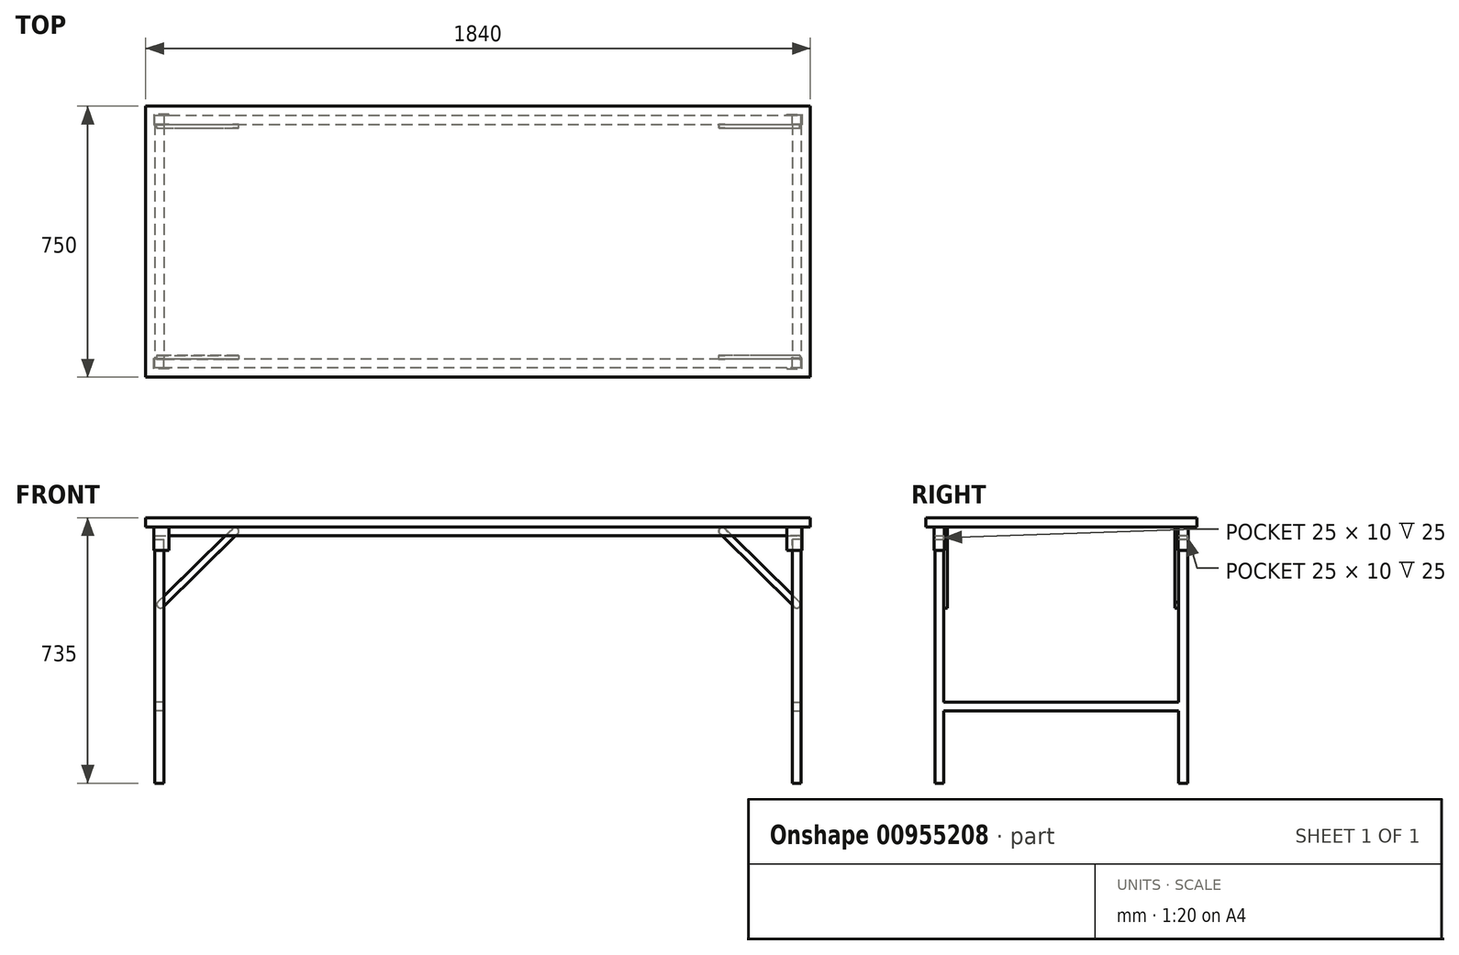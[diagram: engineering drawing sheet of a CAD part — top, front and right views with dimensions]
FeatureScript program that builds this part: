
annotation { "Feature Type Name" : "Feature", "Feature Type Description" : "" }
export const myFeature = defineFeature(function(context is Context, id is Id, definition is map)
    precondition{}
    {
        {
            var Q0;
            Q0=qCreatedBy(makeId("Top.planeOp"),FACE);
            var sketch = newSketch(context, id + "F0", { "sketchPlane" : qUnion([Q0])});
            skLineSegment(sketch, "E0.bottom", {"start": v(0, 0) * mm, "end": v(-1840, 0) * mm});
            skLineSegment(sketch, "E0.top", {"start": v(0, 750) * mm, "end": v(-1840, 750) * mm});
            skLineSegment(sketch, "E0.left", {"start": v(0, 0) * mm, "end": v(0, 750) * mm});
            skLineSegment(sketch, "E0.right", {"start": v(-1840, 0) * mm, "end": v(-1840, 750) * mm});
            skSolve(sketch);
        }
        {
            var Q0;
            Q0=makeQuery(id+"F0.imprint","IMPRINT",FACE,{"disambiguationData":[TD([[makeQuery(id+"F0.imprint","IMPRINT",EDGE,{"derivedFrom":sQuery(id+"F0.wireOp",EDGE,"E0.bottom")}),-1.0]])]});
            extrude(context, id + "F1", {"entities" : qUnion([Q0]), "depth" : 25 * mm, "offsetDistance" : 25 * mm});
        }
        {
            var Q0;
            Q0=makeQuery(id+"F1.opExtrude","CAP_FACE",FACE,{"disambiguationData":[OSD([sQuery(id+"F0.wireOp",EDGE,"E0.bottom"),sQuery(id+"F0.wireOp",EDGE,"E0.top"),sQuery(id+"F0.wireOp",EDGE,"E0.left"),sQuery(id+"F0.wireOp",EDGE,"E0.right")])],"isStart":true});
            var sketch = newSketch(context, id + "F2", { "sketchPlane" : qUnion([Q0])});
            skLineSegment(sketch, "E1.bottom", {"start": v(-25, -25) * mm, "end": v(-1815, -25) * mm});
            skLineSegment(sketch, "E1.top", {"start": v(-25, -50) * mm, "end": v(-1815, -50) * mm});
            skLineSegment(sketch, "E1.left", {"start": v(-25, -25) * mm, "end": v(-25, -50) * mm});
            skLineSegment(sketch, "E1.right", {"start": v(-1815, -25) * mm, "end": v(-1815, -50) * mm});
            skLineSegment(sketch, "E2.bottom", {"start": v(-1815, -700) * mm, "end": v(-25, -700) * mm});
            skLineSegment(sketch, "E2.top", {"start": v(-1815, -725) * mm, "end": v(-25, -725) * mm});
            skLineSegment(sketch, "E2.left", {"start": v(-1815, -700) * mm, "end": v(-1815, -725) * mm});
            skLineSegment(sketch, "E2.right", {"start": v(-25, -700) * mm, "end": v(-25, -725) * mm});
            skSolve(sketch);
        }
        {
            var Q0;
            Q0=qSketchRegion(id+"F2",true);
            extrude(context, id + "F3", {"entities" : qUnion([Q0]), "operationType" : NewBodyOperationType.ADD, "depth" : 25 * mm, "offsetDistance" : 25 * mm});
        }
        {
            var Q0;
            Q0=makeQuery(id+"F1.opExtrude","CAP_FACE",FACE,{"disambiguationData":[OSD([sQuery(id+"F0.wireOp",EDGE,"E0.bottom"),sQuery(id+"F0.wireOp",EDGE,"E0.top"),sQuery(id+"F0.wireOp",EDGE,"E0.left"),sQuery(id+"F0.wireOp",EDGE,"E0.right")])],"isStart":true});
            var sketch = newSketch(context, id + "F4", { "sketchPlane" : qUnion([Q0])});
            skLineSegment(sketch, "E3", {"start": v(-25, -25) * mm, "end": v(-65, -25) * mm});
            skLineSegment(sketch, "E4", {"start": v(-65, -25) * mm, "end": v(-65, -23) * mm});
            skLineSegment(sketch, "E5", {"start": v(-65, -23) * mm, "end": v(-23, -23) * mm});
            skLineSegment(sketch, "E6", {"start": v(-23, -23) * mm, "end": v(-23, -52) * mm});
            skLineSegment(sketch, "E7", {"start": v(-23, -52) * mm, "end": v(-65, -52) * mm});
            skLineSegment(sketch, "E8", {"start": v(-65, -52) * mm, "end": v(-65, -50) * mm});
            skLineSegment(sketch, "E9", {"start": v(-65, -50) * mm, "end": v(-25, -50) * mm});
            skLineSegment(sketch, "E10", {"start": v(-25, -50) * mm, "end": v(-25, -25) * mm});
            skSolve(sketch);
        }
        {
            var Q0;
            Q0=makeQuery(id+"F4.imprint","IMPRINT",FACE,{"disambiguationData":[TD([[makeQuery(id+"F4.imprint","IMPRINT",EDGE,{"derivedFrom":sQuery(id+"F4.wireOp",EDGE,"E3")}),-1.0]])]});
            extrude(context, id + "F5", {"entities" : qUnion([Q0]), "operationType" : NewBodyOperationType.ADD, "depth" : 65 * mm, "offsetDistance" : 25 * mm});
        }
        {
            var Q0;
            Q0=makeQuery(id+"F3.opExtrude","CAP_FACE",FACE,{"disambiguationData":[OSD([sQuery(id+"F2.wireOp",EDGE,"E1.bottom"),sQuery(id+"F2.wireOp",EDGE,"E1.top"),sQuery(id+"F2.wireOp",EDGE,"E1.left"),sQuery(id+"F2.wireOp",EDGE,"E1.right")])],"isStart":false});
            cPlane(context, id + "F6", {"entities" : qUnion([Q0]), "cplaneType" : CPlaneType.OFFSET, "offset" : 10 * mm, "width" : 150 * mm, "height" : 150 * mm});
        }
        {
            var Q0;
            Q0=qCreatedBy(id+"F6.planeOp",FACE);
            var sketch = newSketch(context, id + "F7", { "sketchPlane" : qUnion([Q0])});
            skLineSegment(sketch, "E11.bottom", {"start": v(-25, -25.02) * mm, "end": v(-50, -25.02) * mm});
            skLineSegment(sketch, "E11.top", {"start": v(-25, -50.02) * mm, "end": v(-50, -50.02) * mm});
            skLineSegment(sketch, "E11.left", {"start": v(-25, -25.02) * mm, "end": v(-25, -50.02) * mm});
            skLineSegment(sketch, "E11.right", {"start": v(-50, -25.02) * mm, "end": v(-50, -50.02) * mm});
            skSolve(sketch);
        }
        {
            var Q0;
            Q0=makeQuery(id+"F7.imprint","IMPRINT",FACE,{"disambiguationData":[TD([[makeQuery(id+"F7.imprint","IMPRINT",EDGE,{"derivedFrom":sQuery(id+"F7.wireOp",EDGE,"E11.bottom")}),1.0]])]});
            extrude(context, id + "F8", {"entities" : qUnion([Q0]), "operationType" : NewBodyOperationType.ADD, "depth" : 675 * mm, "offsetDistance" : 25 * mm});
        }
        {
            var Q0;
            Q0=makeQuery(id+"F0.imprint","IMPRINT",FACE,{"disambiguationData":[TD([[makeQuery(id+"F0.imprint","IMPRINT",EDGE,{"derivedFrom":sQuery(id+"F0.wireOp",EDGE,"E0.bottom")}),-1.0]])]});
            var sketch = newSketch(context, id + "F9", { "sketchPlane" : qUnion([Q0])});
            skLineSegment(sketch, "E12", {"start": v(-1815, 25) * mm, "end": v(-1775, 25) * mm});
            skLineSegment(sketch, "E13", {"start": v(-1775, 25) * mm, "end": v(-1775, 23) * mm});
            skLineSegment(sketch, "E14", {"start": v(-1775, 23) * mm, "end": v(-1817, 23) * mm});
            skLineSegment(sketch, "E15", {"start": v(-1817, 23) * mm, "end": v(-1817, 52) * mm});
            skLineSegment(sketch, "E16", {"start": v(-1817, 52) * mm, "end": v(-1775, 52) * mm});
            skLineSegment(sketch, "E17", {"start": v(-1775, 52) * mm, "end": v(-1775, 50) * mm});
            skLineSegment(sketch, "E18", {"start": v(-1775, 50) * mm, "end": v(-1815, 50) * mm});
            skLineSegment(sketch, "E19", {"start": v(-1815, 50) * mm, "end": v(-1815, 25) * mm});
            skLineSegment(sketch, "E20.MirrorCS", {"start": v(-1775, 725) * mm, "end": v(-1775, 727) * mm});
            skLineSegment(sketch, "E21.MirrorCS", {"start": v(-1775, 698) * mm, "end": v(-1775, 700) * mm});
            skLineSegment(sketch, "E22.MirrorCS", {"start": v(-1817, 698) * mm, "end": v(-1775, 698) * mm});
            skLineSegment(sketch, "E23.MirrorCS", {"start": v(-1775, 700) * mm, "end": v(-1815, 700) * mm});
            skLineSegment(sketch, "E24.MirrorCS", {"start": v(-1815, 725) * mm, "end": v(-1775, 725) * mm});
            skLineSegment(sketch, "E25.MirrorCS", {"start": v(-1775, 727) * mm, "end": v(-1817, 727) * mm});
            skLineSegment(sketch, "E26.MirrorCS", {"start": v(-1817, 727) * mm, "end": v(-1817, 698) * mm});
            skLineSegment(sketch, "E27.MirrorCS", {"start": v(-1815, 700) * mm, "end": v(-1815, 725) * mm});
            skLineSegment(sketch, "E28.MirrorCS", {"start": v(-65.05, 724.98) * mm, "end": v(-65.05, 726.98) * mm});
            skLineSegment(sketch, "E29.MirrorCS", {"start": v(-65.05, 697.98) * mm, "end": v(-65.05, 699.98) * mm});
            skLineSegment(sketch, "E30.MirrorCS", {"start": v(-23.05, 726.98) * mm, "end": v(-23.05, 697.98) * mm});
            skLineSegment(sketch, "E31.MirrorCS", {"start": v(-65.05, 699.98) * mm, "end": v(-25.05, 699.98) * mm});
            skLineSegment(sketch, "E32.MirrorCS", {"start": v(-25.05, 699.98) * mm, "end": v(-25.05, 724.98) * mm});
            skLineSegment(sketch, "E33.MirrorCS", {"start": v(-65.05, 726.98) * mm, "end": v(-23.05, 726.98) * mm});
            skLineSegment(sketch, "E34.MirrorCS", {"start": v(-25.05, 724.98) * mm, "end": v(-65.05, 724.98) * mm});
            skLineSegment(sketch, "E35.MirrorCS", {"start": v(-23.05, 697.98) * mm, "end": v(-65.05, 697.98) * mm});
            skSolve(sketch);
        }
        {
            var Q0;
            Q0=makeQuery(id+"F9.imprint","IMPRINT",FACE,{"disambiguationData":[TD([[makeQuery(id+"F9.imprint","IMPRINT",EDGE,{"derivedFrom":sQuery(id+"F9.wireOp",EDGE,"E20.MirrorCS")}),1.0]])]});
            var Q1;
            Q1=makeQuery(id+"F9.imprint","IMPRINT",FACE,{"disambiguationData":[TD([[makeQuery(id+"F9.imprint","IMPRINT",EDGE,{"derivedFrom":sQuery(id+"F9.wireOp",EDGE,"E28.MirrorCS")}),-1.0]])]});
            var Q2;
            Q2=makeQuery(id+"F9.imprint","IMPRINT",FACE,{"disambiguationData":[TD([[makeQuery(id+"F9.imprint","IMPRINT",EDGE,{"derivedFrom":sQuery(id+"F9.wireOp",EDGE,"E12")}),-1.0]])]});
            extrude(context, id + "F10", {"entities" : qUnion([Q0, Q1, Q2]), "operationType" : NewBodyOperationType.ADD, "oppositeDirection" : true, "depth" : 65 * mm, "offsetDistance" : 25 * mm});
        }
        {
            var Q0;
            Q0=makeQuery(id+"F3.opExtrude","CAP_FACE",FACE,{"disambiguationData":[OSD([sQuery(id+"F2.wireOp",EDGE,"E1.bottom"),sQuery(id+"F2.wireOp",EDGE,"E1.top"),sQuery(id+"F2.wireOp",EDGE,"E1.left"),sQuery(id+"F2.wireOp",EDGE,"E1.right")])],"isStart":false});
            cPlane(context, id + "F11", {"entities" : qUnion([Q0]), "cplaneType" : CPlaneType.OFFSET, "offset" : 10 * mm, "width" : 150 * mm, "height" : 150 * mm});
        }
        {
            var Q0;
            Q0=qCreatedBy(id+"F11.planeOp",FACE);
            var sketch = newSketch(context, id + "F12", { "sketchPlane" : qUnion([Q0])});
            skLineSegment(sketch, "E36.bottom", {"start": v(-1790, -25) * mm, "end": v(-1815, -25) * mm});
            skLineSegment(sketch, "E36.top", {"start": v(-1790, -50) * mm, "end": v(-1815, -50) * mm});
            skLineSegment(sketch, "E36.left", {"start": v(-1790, -25) * mm, "end": v(-1790, -50) * mm});
            skLineSegment(sketch, "E36.right", {"start": v(-1815, -25) * mm, "end": v(-1815, -50) * mm});
            skSolve(sketch);
        }
        {
            var Q0;
            Q0=makeQuery(id+"F12.imprint","IMPRINT",FACE,{"disambiguationData":[TD([[makeQuery(id+"F12.imprint","IMPRINT",EDGE,{"derivedFrom":sQuery(id+"F12.wireOp",EDGE,"E36.bottom")}),1.0]])]});
            extrude(context, id + "F13", {"entities" : qUnion([Q0]), "operationType" : NewBodyOperationType.ADD, "depth" : 675 * mm, "offsetDistance" : 25 * mm});
        }
        {
            var Q0;
            Q0=makeQuery(id+"F3.opExtrude","CAP_FACE",FACE,{"disambiguationData":[OSD([sQuery(id+"F2.wireOp",EDGE,"E2.bottom"),sQuery(id+"F2.wireOp",EDGE,"E2.top"),sQuery(id+"F2.wireOp",EDGE,"E2.left"),sQuery(id+"F2.wireOp",EDGE,"E2.right")])],"isStart":false});
            cPlane(context, id + "F14", {"entities" : qUnion([Q0]), "cplaneType" : CPlaneType.OFFSET, "offset" : 10 * mm, "width" : 150 * mm, "height" : 150 * mm});
        }
        {
            var Q0;
            Q0=qCreatedBy(id+"F14.planeOp",FACE);
            var sketch = newSketch(context, id + "F15", { "sketchPlane" : qUnion([Q0])});
            skLineSegment(sketch, "E37.bottom", {"start": v(-25, -700) * mm, "end": v(-50, -700) * mm});
            skLineSegment(sketch, "E37.top", {"start": v(-25, -725) * mm, "end": v(-50, -725) * mm});
            skLineSegment(sketch, "E37.left", {"start": v(-25, -700) * mm, "end": v(-25, -725) * mm});
            skLineSegment(sketch, "E37.right", {"start": v(-50, -700) * mm, "end": v(-50, -725) * mm});
            skLineSegment(sketch, "E38.bottom", {"start": v(-1815, -725) * mm, "end": v(-1790, -725) * mm});
            skLineSegment(sketch, "E38.top", {"start": v(-1815, -700) * mm, "end": v(-1790, -700) * mm});
            skLineSegment(sketch, "E38.left", {"start": v(-1815, -725) * mm, "end": v(-1815, -700) * mm});
            skLineSegment(sketch, "E38.right", {"start": v(-1790, -725) * mm, "end": v(-1790, -700) * mm});
            skSolve(sketch);
        }
        {
            var Q0;
            Q0=qSketchRegion(id+"F15",true);
            extrude(context, id + "F16", {"entities" : qUnion([Q0]), "operationType" : NewBodyOperationType.ADD, "depth" : 675 * mm, "offsetDistance" : 25 * mm});
        }
        {
            var Q0;
            Q0=makeQuery(id+"F8.opExtrude","SWEPT_FACE",FACE,{"disambiguationData":[OSD([sQuery(id+"F7.wireOp",EDGE,"E11.top")])]});
            cPlane(context, id + "F17", {"entities" : qUnion([Q0]), "cplaneType" : CPlaneType.OFFSET, "offset" : 0 * mm, "width" : 150 * mm, "height" : 150 * mm});
        }
        {
            var Q0;
            Q0=qCreatedBy(id+"F17.planeOp",FACE);
            var sketch = newSketch(context, id + "F18", { "sketchPlane" : qUnion([Q0])});
            skLineSegment(sketch, "E39.bottom", {"start": v(25, -485) * mm, "end": v(50, -485) * mm});
            skLineSegment(sketch, "E39.top", {"start": v(25, -510) * mm, "end": v(50, -510) * mm});
            skLineSegment(sketch, "E39.left", {"start": v(25, -485) * mm, "end": v(25, -510) * mm});
            skLineSegment(sketch, "E39.right", {"start": v(50, -485) * mm, "end": v(50, -510) * mm});
            skSolve(sketch);
        }
        {
            var Q0;
            Q0=makeQuery(id+"F18.imprint","IMPRINT",FACE,{"disambiguationData":[TD([[makeQuery(id+"F18.imprint","IMPRINT",EDGE,{"derivedFrom":sQuery(id+"F18.wireOp",EDGE,"E39.bottom")}),-1.0]])]});
            extrude(context, id + "F19", {"entities" : qUnion([Q0]), "operationType" : NewBodyOperationType.ADD, "depth" : 650 * mm, "offsetDistance" : 25 * mm});
        }
        {
            var Q0;
            Q0=makeQuery(id+"F13.opExtrude","SWEPT_FACE",FACE,{"disambiguationData":[OSD([sQuery(id+"F12.wireOp",EDGE,"E36.top")])]});
            cPlane(context, id + "F20", {"entities" : qUnion([Q0]), "cplaneType" : CPlaneType.OFFSET, "offset" : 0 * mm, "width" : 150 * mm, "height" : 150 * mm});
        }
        {
            var Q0;
            Q0=qCreatedBy(id+"F20.planeOp",FACE);
            var sketch = newSketch(context, id + "F21", { "sketchPlane" : qUnion([Q0])});
            skLineSegment(sketch, "E40.0", {"start": v(1790, -710) * mm, "end": v(1790, -65) * mm});
            skLineSegment(sketch, "E41.0.0", {"start": v(1815, -65) * mm, "end": v(1790, -65) * mm});
            skLineSegment(sketch, "E41.0.1", {"start": v(1790, -65) * mm, "end": v(1790, -710) * mm});
            skLineSegment(sketch, "E41.0.2", {"start": v(1790, -710) * mm, "end": v(1815, -710) * mm});
            skLineSegment(sketch, "E41.0.3", {"start": v(1815, -710) * mm, "end": v(1815, -65) * mm});
            skLineSegment(sketch, "E42.bottom", {"start": v(1790, -485) * mm, "end": v(1815, -485) * mm});
            skLineSegment(sketch, "E42.top", {"start": v(1790, -510) * mm, "end": v(1815, -510) * mm});
            skLineSegment(sketch, "E42.left", {"start": v(1790, -485) * mm, "end": v(1790, -510) * mm});
            skLineSegment(sketch, "E42.right", {"start": v(1815, -485) * mm, "end": v(1815, -510) * mm});
            skSolve(sketch);
        }
        {
            var Q0;
            Q0=makeQuery(id+"F21.imprint","IMPRINT",FACE,{"disambiguationData":[TD([[makeQuery(id+"F21.imprint","IMPRINT",EDGE,{"derivedFrom":sQuery(id+"F21.wireOp",EDGE,"E42.bottom")}),-1.0]])]});
            extrude(context, id + "F22", {"entities" : qUnion([Q0]), "operationType" : NewBodyOperationType.ADD, "depth" : 650 * mm, "offsetDistance" : 25 * mm});
        }
        {
            var Q0;
            {var subQ0=sQuery(id+"F9.wireOp",EDGE,"E32.MirrorCS");var subQ3=sQuery(id+"F15.wireOp",EDGE,"E37.bottom");Q0=makeQuery(id+"F19.boolean.opBoolean","SPLIT",FACE,{"disambiguationData":[TD([makeQuery(id+"F10.opExtrude","SWEPT_FACE",FACE,{"disambiguationData":[OSD([subQ0])]})])],"derivedFrom":makeQuery(id+"F16.opExtrude","SWEPT_FACE",FACE,{"disambiguationData":[OSD([subQ3])]})});}
            var sketch = newSketch(context, id + "F23", { "sketchPlane" : qUnion([Q0])});
            skPoint(sketch, "E43", {"position": v(-37.5, -215) * mm});
            skPoint(sketch, "E44", {"position": v(-243.05, -12.5) * mm});
            skLineSegment(sketch, "E45", {"start": v(-236.03, -5.38) * mm, "end": v(-29.52, -208.98) * mm});
            skLineSegment(sketch, "E46", {"start": v(-251.03, -18.52) * mm, "end": v(-44.52, -222.12) * mm});
            skArc(sketch, "E47", {"start": v(-44.52, -222.12) * mm, "mid": v(-30.91, -222.52) * mm, "end": v(-29.52, -208.98) * mm});
            skArc(sketch, "E48", {"start": v(-236.03, -5.38) * mm, "mid": v(-249.64, -4.98) * mm, "end": v(-251.03, -18.52) * mm});
            skSolve(sketch);
        }
        {
            var Q0;
            {var subQ0=sQuery(id+"F23.wireOp",EDGE,"E48");Q0=makeQuery(id+"F23.imprint","IMPRINT",FACE,{"disambiguationData":[TD([[makeQuery(id+"F23.imprint","IMPRINT",EDGE,{"derivedFrom":subQ0}),1.0]])]});}
            var Q1;
            {var subQ0=sQuery(id+"F23.wireOp",EDGE,"E47");Q1=makeQuery(id+"F23.imprint","IMPRINT",FACE,{"disambiguationData":[TD([[makeQuery(id+"F23.imprint","IMPRINT",EDGE,{"derivedFrom":subQ0}),1.0]])]});}
            extrude(context, id + "F24", {"entities" : qUnion([Q0, Q1]), "operationType" : NewBodyOperationType.ADD, "depth" : 10 * mm, "offsetDistance" : 25 * mm});
        }
        {
            var Q0;
            Q0=makeQuery(id+"F19.boolean.opBoolean","SPLIT",FACE,{"disambiguationData":[TD([makeQuery(id+"F19.opExtrude","SWEPT_FACE",FACE,{"disambiguationData":[OSD([sQuery(id+"F18.wireOp",EDGE,"E39.bottom")])]})])],"derivedFrom":makeQuery(id+"F8.opExtrude","SWEPT_FACE",FACE,{"disambiguationData":[OSD([sQuery(id+"F7.wireOp",EDGE,"E11.top")])]})});
            var sketch = newSketch(context, id + "F25", { "sketchPlane" : qUnion([Q0])});
            skPoint(sketch, "E49", {"position": v(37.5, -215) * mm});
            skPoint(sketch, "E50", {"position": v(243, -12.5) * mm});
            skLineSegment(sketch, "E51", {"start": v(44.52, -222.12) * mm, "end": v(250.98, -18.46) * mm});
            skLineSegment(sketch, "E52", {"start": v(30.48, -207.88) * mm, "end": v(236.93, -4.22) * mm});
            skLineSegment(sketch, "E53", {"start": v(43.27, -207.6) * mm, "end": v(43.27, -207.6) * mm});
            skArc(sketch, "E54", {"start": v(30.48, -207.88) * mm, "mid": v(30.38, -222.02) * mm, "end": v(44.52, -222.12) * mm});
            skArc(sketch, "E55", {"start": v(250.98, -18.46) * mm, "mid": v(251.08, -4.32) * mm, "end": v(236.93, -4.22) * mm});
            skSolve(sketch);
        }
        {
            var Q0;
            {var subQ0=sQuery(id+"F25.wireOp",EDGE,"E55");Q0=makeQuery(id+"F25.imprint","IMPRINT",FACE,{"disambiguationData":[TD([[makeQuery(id+"F25.imprint","IMPRINT",EDGE,{"derivedFrom":subQ0}),1.0]])]});}
            var Q1;
            {var subQ0=sQuery(id+"F25.wireOp",EDGE,"E54");Q1=makeQuery(id+"F25.imprint","IMPRINT",FACE,{"disambiguationData":[TD([[makeQuery(id+"F25.imprint","IMPRINT",EDGE,{"derivedFrom":subQ0}),1.0]])]});}
            extrude(context, id + "F26", {"entities" : qUnion([Q0, Q1]), "depth" : 10 * mm, "offsetDistance" : 25 * mm});
        }
        {
            var Q0;
            {var subQ0=sQuery(id+"F21.wireOp",EDGE,"E41.0.0");Q0=makeQuery(id+"F21.imprint","IMPRINT",FACE,{"disambiguationData":[TD([[makeQuery(id+"F21.imprint","IMPRINT",EDGE,{"derivedFrom":subQ0}),1.0]])]});}
            var sketch = newSketch(context, id + "F27", { "sketchPlane" : qUnion([Q0])});
            skLineSegment(sketch, "E56", {"start": v(1806.27, -207.85) * mm, "end": v(1599, -5.04) * mm});
            skLineSegment(sketch, "E57", {"start": v(1585, -19.33) * mm, "end": v(1792.29, -222.15) * mm});
            skArc(sketch, "E58", {"start": v(1792.29, -222.15) * mm, "mid": v(1806.43, -222) * mm, "end": v(1806.27, -207.85) * mm});
            skArc(sketch, "E59", {"start": v(1599, -5.04) * mm, "mid": v(1584.85, -5.19) * mm, "end": v(1585, -19.33) * mm});
            skSolve(sketch);
        }
        {
            var Q0;
            {var subQ0=sQuery(id+"F27.wireOp",EDGE,"E58");Q0=makeQuery(id+"F27.imprint","IMPRINT",FACE,{"disambiguationData":[TD([[makeQuery(id+"F27.imprint","IMPRINT",EDGE,{"derivedFrom":subQ0}),1.0]])]});}
            var Q1;
            {var subQ0=sQuery(id+"F27.wireOp",EDGE,"E59");Q1=makeQuery(id+"F27.imprint","IMPRINT",FACE,{"disambiguationData":[TD([[makeQuery(id+"F27.imprint","IMPRINT",EDGE,{"derivedFrom":subQ0}),1.0]])]});}
            extrude(context, id + "F28", {"entities" : qUnion([Q0, Q1]), "operationType" : NewBodyOperationType.ADD, "depth" : 10 * mm, "offsetDistance" : 25 * mm});
        }
        {
            var Q0;
            {var subQ0=sQuery(id+"F9.wireOp",EDGE,"E23.MirrorCS");Q0=makeQuery(id+"F22.boolean.opBoolean","SPLIT",FACE,{"disambiguationData":[TD([makeQuery(id+"F10.opExtrude","SWEPT_FACE",FACE,{"disambiguationData":[OSD([subQ0])]})])],"derivedFrom":makeQuery(id+"F16.opExtrude","SWEPT_FACE",FACE,{"disambiguationData":[OSD([sQuery(id+"F15.wireOp",EDGE,"E38.top")])]})});}
            var sketch = newSketch(context, id + "F29", { "sketchPlane" : qUnion([Q0])});
            skPoint(sketch, "E60", {"position": v(-1799.28, -215) * mm});
            skPoint(sketch, "E61", {"position": v(-1591.95, -12.12) * mm});
            skLineSegment(sketch, "E62", {"start": v(-1806.3, -207.88) * mm, "end": v(-1599.02, -5.07) * mm});
            skLineSegment(sketch, "E63", {"start": v(-1792.33, -222.18) * mm, "end": v(-1585.04, -19.37) * mm});
            skArc(sketch, "E64", {"start": v(-1585.04, -19.37) * mm, "mid": v(-1584.88, -5.23) * mm, "end": v(-1599.02, -5.07) * mm});
            skArc(sketch, "E65", {"start": v(-1806.3, -207.88) * mm, "mid": v(-1806.46, -222.02) * mm, "end": v(-1792.33, -222.18) * mm});
            skSolve(sketch);
        }
        {
            var Q0;
            {var subQ0=sQuery(id+"F29.wireOp",EDGE,"E64");Q0=makeQuery(id+"F29.imprint","IMPRINT",FACE,{"disambiguationData":[TD([[makeQuery(id+"F29.imprint","IMPRINT",EDGE,{"derivedFrom":subQ0}),1.0]])]});}
            var Q1;
            {var subQ0=sQuery(id+"F29.wireOp",EDGE,"E65");Q1=makeQuery(id+"F29.imprint","IMPRINT",FACE,{"disambiguationData":[TD([[makeQuery(id+"F29.imprint","IMPRINT",EDGE,{"derivedFrom":subQ0}),1.0]])]});}
            extrude(context, id + "F30", {"entities" : qUnion([Q0, Q1]), "operationType" : NewBodyOperationType.ADD, "depth" : 10 * mm, "offsetDistance" : 25 * mm});
        }
    });
